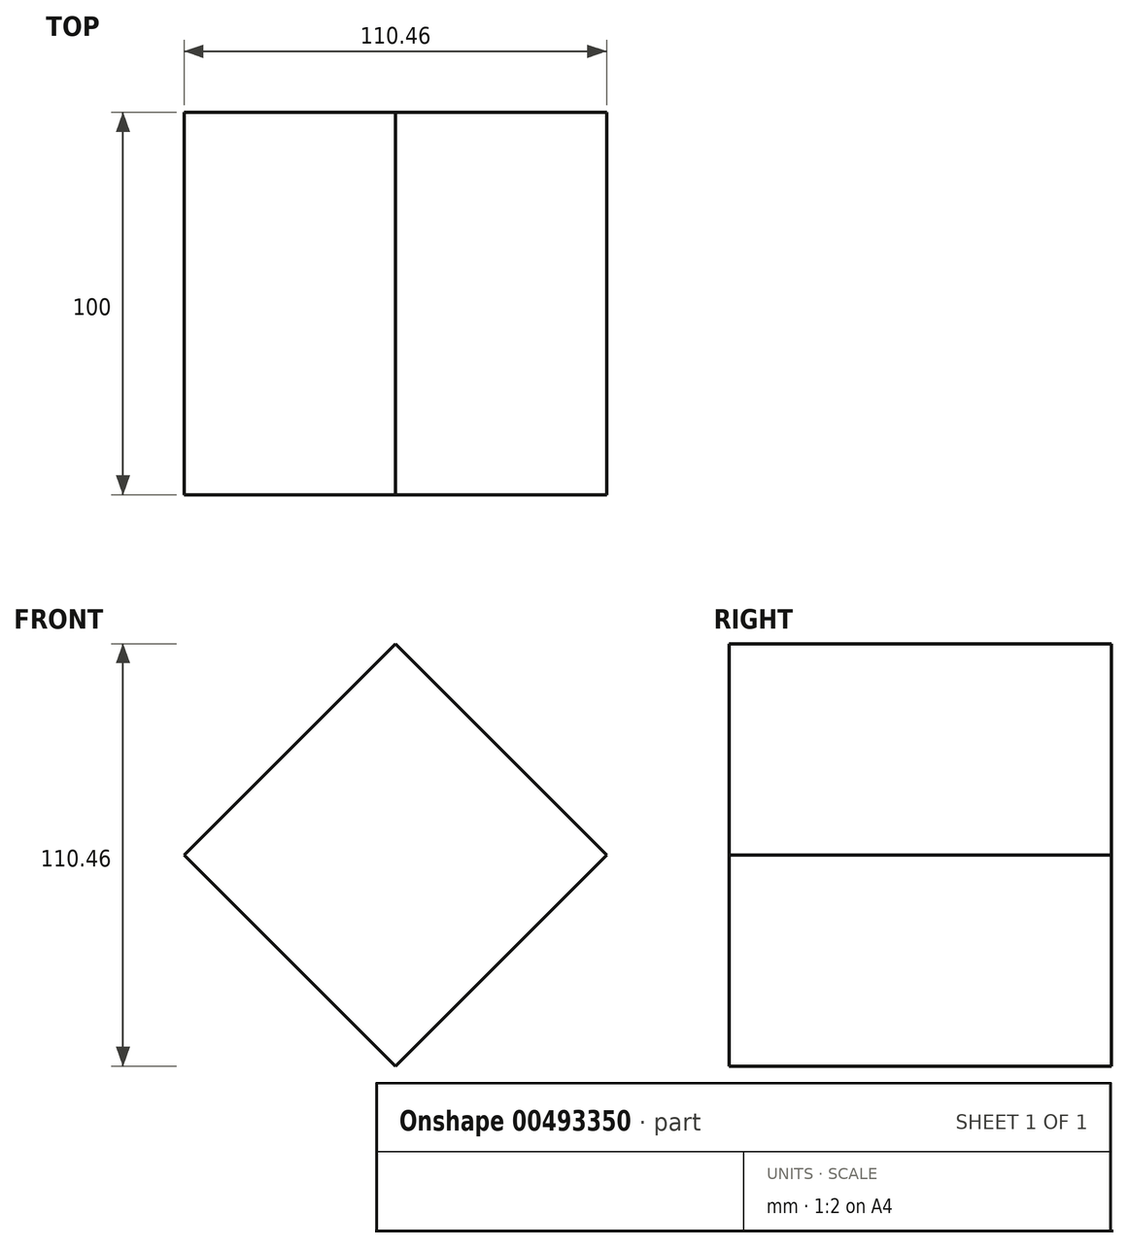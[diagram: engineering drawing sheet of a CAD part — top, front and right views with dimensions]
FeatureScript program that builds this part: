
annotation { "Feature Type Name" : "Feature", "Feature Type Description" : "" }
export const myFeature = defineFeature(function(context is Context, id is Id, definition is map)
    precondition{}
    {
        {
            var Q0;
            Q0=qCreatedBy(makeId("Front.planeOp"),FACE);
            var sketch = newSketch(context, id + "F0", { "sketchPlane" : qUnion([Q0])});
            skCircle(sketch, "E0.cCircle", {"center": v(0, 0) * mm, "radius": 55.23 * mm, "construction": true});
            skLineSegment(sketch, "E0.0", {"start": v(0, 55.23) * mm, "end": v(55.23, 0) * mm});
            skLineSegment(sketch, "E0.1", {"start": v(55.23, 0) * mm, "end": v(0, -55.23) * mm});
            skLineSegment(sketch, "E0.2", {"start": v(0, -55.23) * mm, "end": v(-55.23, 0) * mm});
            skLineSegment(sketch, "E0.3", {"start": v(-55.23, 0) * mm, "end": v(0, 55.23) * mm});
            skSolve(sketch);
        }
        {
            var Q0;
            Q0 = qSketchRegion(id + "F0", true);
            extrude(context, id + "F1", {"entities" : qUnion([Q0]), "endBound" : BoundingType.SYMMETRIC, "depth" : 100 * mm});
        }
    });
